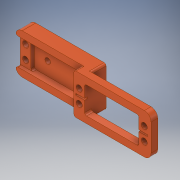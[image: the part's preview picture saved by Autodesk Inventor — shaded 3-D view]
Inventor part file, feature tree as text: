
AUTODESK INVENTOR PART (.ipt)
format: ipt  version: 2017 (Build 210142000, 142)  size: 249,344 bytes
history: native  units: mm
features: extrude x7, sketch x5, fillet x2
ambient origin geometry x8: Origin, YZ Plane, XZ Plane, XY Plane, X Axis, Y Axis, Z Axis, Center Point
bodies: Solid1 (feature_tree)
feature tree (14):
  extrude  "Extrusion1"  Depth=8.0mm
  sketch  "Sketch4"  dims[d2=5.0mm d3=49.5mm]
  extrude  "Extrusion3"  Depth=49.5mm
  sketch  "Sketch5"  dims[d4=49.5mm d5=6.0mm]
  extrude  "Extrusion4"  Depth=6.0mm
  extrude  "Extrusion5"  TaperAngle=0.0deg  [1 undecoded]
  extrude  "Extrusion6"  Depth=5.0mm
  fillet  "Fillet1"  Radius=4.0mm
  extrude  "Extrusion7"  Depth=1.5mm
  extrude  "Extrusion8"  Depth=1.5mm
  fillet  "Fillet2"  Radius=2.75mm
  sketch  "Sketch1"  dims[d0=10.0mm d1=8.0mm]
  sketch  "Sketch6"  dims[d6=30.0mm d7=0.0mm]
  sketch  "Sketch7"  dims[d19=5.0mm d20=5.0mm d22=4.0mm d23=4.5mm d25=2.75mm d26=2.75mm d27=4.0mm d28=30.0mm d29=0.0mm d30=5.0mm d31=5.0mm d33=4.5mm d34=4.0mm d35=2.75mm d36=2.75mm d37=30.0mm d38=0.0mm d39=5.0mm d40=0.0mm d41=6.5mm d42=1.2mm d43=2.0mm d44=0.0mm d45=5.0mm d46=4.2mm d47=10.0mm d48=10.0mm d49=0.0mm d50=40.5mm d51=40.5mm d52=2.5mm d53=0.0mm d54=1.5mm]
note: 1 required parameter value undecoded (feature->parameter linkage not recoverable at this tier; creation-order binding heuristic only, values carry confidence <= 0.55)
